# Revit family: Gira_128700
name_source: partatom
category: Electrical Fixtures
revit_build: Autodesk Revit 2017 (Build: 20160225_1515(x64)
units: mm (PartAtom-declared; Revit-internal decimal feet)

## family parameters
Cut with Voids When Loaded = No
Host = Face
Maintain Annotation Orientation = No
Part Type = Normal
Room Calculation Point = No
Round Connector Dimension = Use Diameter
Shared = No

## types (1)
- Audio ctrl.dev. DRA Door communication
    BIM = https://media.live.bim.site 00_REG 6.rfa
    BIMSITE_PRODUCT_ID = 2c913e152b33b86ff14d9ba59fdf835af8299b99
    Cost = 0 $
    Default Elevation = 1219 mm
    Description = Audio ctrl.dev.DRA Door Audio control device,DRA Features: - Control device to supply power to the audio components of the Gira door communication bus. - Power supply of the reverse-polarity protected and short-circuit-proof 2-wire bus. - Self-resetting electronic short-circuit and overload recognition of the operating voltage and the bus connection. - Buttons for system and door opener programming. - LED status indicators for operation, overload, system programming, and door opener programming. - AC 12 V output to supply power to a common door opener. - Permanent AC 12 V output to supply power to a DCS-TC gateway. - Relay output for switching a door opener with its own power supply. - Door opener time continuously adjustable from 1 to 10 seconds.,Notes : - The audio control device is intended to be installed in the sub-distribution. If this is not possible, use a common surface-mounted distributor. - This component enables door communication systems with up to 70 devices to be established (e.g. 1 x built-in loudspeaker, 5 x add-on modules for built-in loudspeakers, 68 x surface-mounted home stations).
    GTIN = 4010337287001
    HAN = 128700
    HeinzeBIM = https://www.heinze.de
    Manufacturer = Gira
    Output voltage [Volt] Number = 12
    URL = https://www.gira.de

## geometry (parser evidence)
native form markers: Blend x2, Sweep x3
no freeform markers — native parametric forms only
